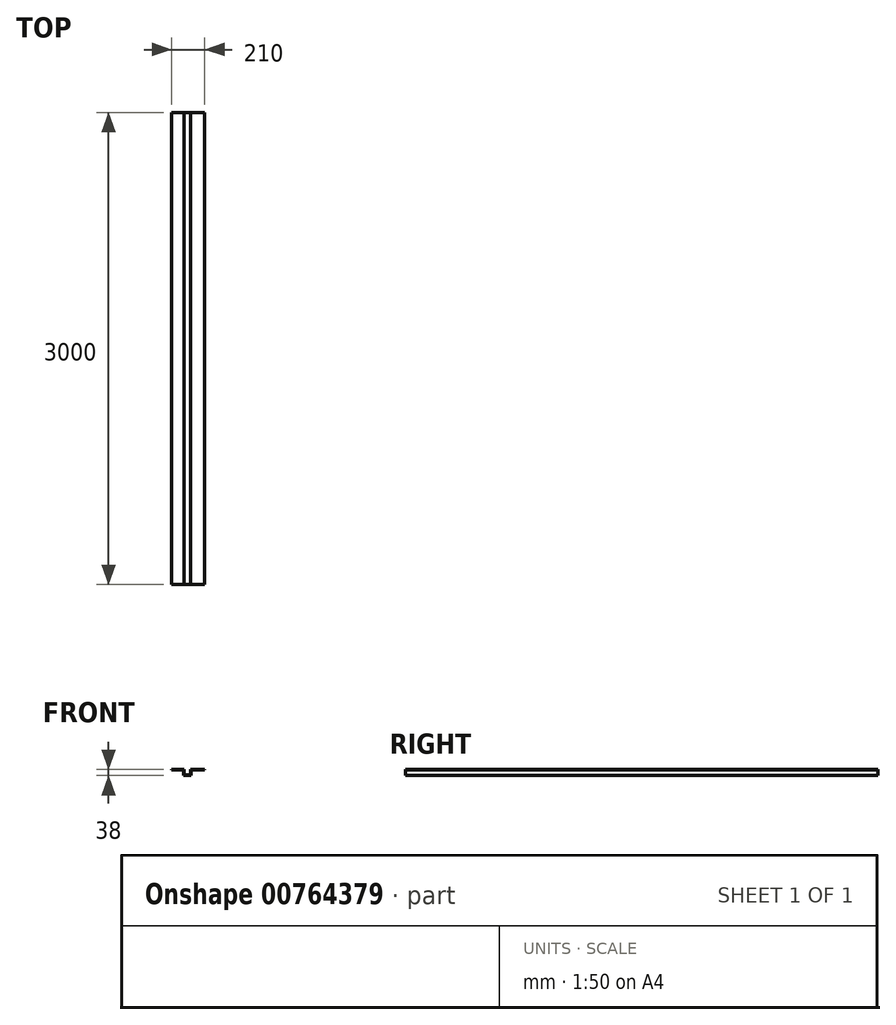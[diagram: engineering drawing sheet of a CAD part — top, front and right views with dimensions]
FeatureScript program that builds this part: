
annotation { "Feature Type Name" : "Feature", "Feature Type Description" : "" }
export const myFeature = defineFeature(function(context is Context, id is Id, definition is map)
    precondition{}
    {
        {
            var Q0;
            Q0=qCreatedBy(makeId("Front.planeOp"),FACE);
            var sketch = newSketch(context, id + "F0", { "sketchPlane" : qUnion([Q0])});
            skLineSegment(sketch, "E0", {"start": v(0, 0) * mm, "end": v(25, 0) * mm});
            skLineSegment(sketch, "E1", {"start": v(25, 0) * mm, "end": v(25, 35) * mm});
            skLineSegment(sketch, "E2.MirrorCS", {"start": v(-25, 0) * mm, "end": v(-25, 35) * mm});
            skLineSegment(sketch, "E3.MirrorCS", {"start": v(0, 0) * mm, "end": v(-25, 0) * mm});
            skLineSegment(sketch, "E4", {"start": v(25, 35) * mm, "end": v(110, 35) * mm});
            skLineSegment(sketch, "E5", {"start": v(-25, 35) * mm, "end": v(-100, 35) * mm});
            skLineSegment(sketch, "E6.0", {"start": v(-22, 38) * mm, "end": v(-100, 38) * mm});
            skLineSegment(sketch, "E6.1", {"start": v(-22, 3) * mm, "end": v(-22, 38) * mm});
            skLineSegment(sketch, "E6.2", {"start": v(22, 38) * mm, "end": v(110, 38) * mm});
            skLineSegment(sketch, "E6.3", {"start": v(22, 3) * mm, "end": v(22, 38) * mm});
            skLineSegment(sketch, "E6.4", {"start": v(0, 3) * mm, "end": v(22, 3) * mm});
            skLineSegment(sketch, "E6.5", {"start": v(0, 3) * mm, "end": v(-22, 3) * mm});
            skLineSegment(sketch, "E7", {"start": v(-100, 38) * mm, "end": v(-100, 35) * mm});
            skLineSegment(sketch, "E8", {"start": v(110, 38) * mm, "end": v(110, 35) * mm});
            skSolve(sketch);
        }
        {
            var Q0;
            Q0=makeQuery(id+"F0.imprint","IMPRINT",FACE,{"disambiguationData":[TD([[makeQuery(id+"F0.imprint","IMPRINT",EDGE,{"derivedFrom":sQuery(id+"F0.wireOp",EDGE,"E0")}),1.0]])]});
            extrude(context, id + "F1", {"entities" : qUnion([Q0]), "depth" : 3000 * mm, "offsetDistance" : 25 * mm, "symmetric" : true});
        }
    });
